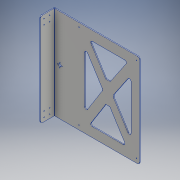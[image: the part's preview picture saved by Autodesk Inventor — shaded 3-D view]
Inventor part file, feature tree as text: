
AUTODESK INVENTOR PART (.ipt)
format: ipt  version: 2017.3 (Build 213256000, 256)  size: 303,616 bytes
history: native  units: mm
features: other x5, sketch x4, sheet_metal_op x3, chamfer x2, mirror x1, hole x1
ambient origin geometry x8: Origin, YZ Plane, XZ Plane, XY Plane, X Axis, Y Axis, Z Axis, Center Point
bodies: Solid1 (feature_tree)
feature tree (16):
  sheet_metal_op  "Contour Flange1"
  mirror  "Mirror1"
  chamfer  "Corner Round1"
  hole  "Hole1"  [1 undecoded]
  chamfer  "Corner Round2"
  sketch  "Sketch1"  dims[d0=50.0mm d1=310.0mm]
  other  "Plate1"
  sheet_metal_op  "Bend1"
  sheet_metal_op  "Corner1"
  sketch  "Sketch2"  dims[d2=3.0mm]
  sketch  "Sketch3"  dims[d3=1.5mm]
  sketch  "Sketch4"  dims[d4=6.0mm d5=3.0mm d6=340.0mm d7=0.8mm d8=3.0mm d9=12.0mm d10=3.0mm d11=3.0mm d12=20.0mm d13=12.5mm d14=13.5mm d15=3.2mm d16=3.0mm d17=0.0mm d18=6.0mm d19=10.0mm d20=15.0mm d21=210.0mm d22=310.0mm d23=3.0mm d24=3.2mm d25=6.0mm d26=4.0mm d27=2.0mm d28=90.0deg d29=3.0mm d30=20.594885mm d31=15.0mm d32=10.0mm d33=310.0mm d34=210.0mm d36=20.0mm d37=20.0mm d40=30.0mm d42=80.0mm d43=40.0mm d44=30.0mm d45=30.0mm d46=3.0mm d47=0.0mm d48=6.0mm d49=19.5mm d50=10.2mm d51=3.0mm d52=0.0mm d54=2.5mm d55=16.0mm d56=170.0mm]
  other  "Cut1"
  other  "Cut2"
  other  "Cut3"
  other  "Definition1"
note: 1 required parameter value undecoded (feature->parameter linkage not recoverable at this tier; creation-order binding heuristic only, values carry confidence <= 0.55)
